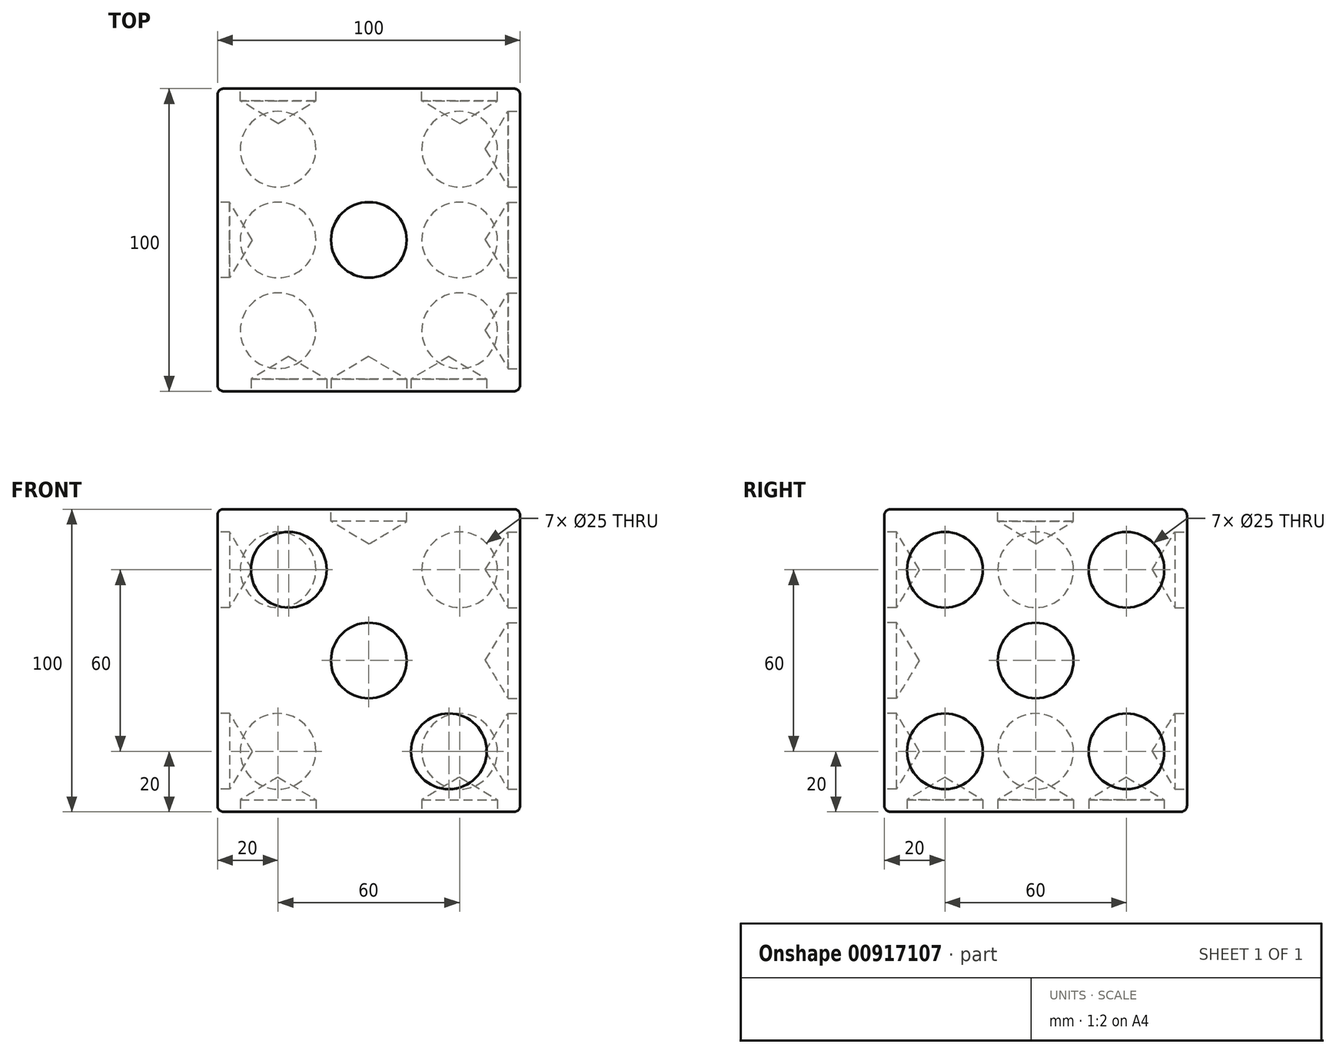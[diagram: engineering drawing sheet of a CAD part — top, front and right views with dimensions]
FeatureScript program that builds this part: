
annotation { "Feature Type Name" : "Feature", "Feature Type Description" : "" }
export const myFeature = defineFeature(function(context is Context, id is Id, definition is map)
    precondition{}
    {
        {
            var Q0;
            Q0=qCreatedBy(makeId("Top.planeOp"),FACE);
            var sketch = newSketch(context, id + "F0", { "sketchPlane" : qUnion([Q0])});
            skLineSegment(sketch, "E0.bottom", {"start": v(50, -50) * mm, "end": v(-50, -50) * mm});
            skLineSegment(sketch, "E0.top", {"start": v(50, 50) * mm, "end": v(-50, 50) * mm});
            skLineSegment(sketch, "E0.left", {"start": v(50, -50) * mm, "end": v(50, 50) * mm});
            skLineSegment(sketch, "E0.right", {"start": v(-50, -50) * mm, "end": v(-50, 50) * mm});
            skPoint(sketch, "E0.middle", {"position": v(0, 0) * mm});
            skSolve(sketch);
        }
        {
            var Q0;
            Q0=makeQuery(id+"F0.imprint","IMPRINT",FACE,{"disambiguationData":[TD([[makeQuery(id+"F0.imprint","IMPRINT",EDGE,{"derivedFrom":sQuery(id+"F0.wireOp",EDGE,"E0.bottom")}),-1.0]])]});
            extrude(context, id + "F1", {"entities" : qUnion([Q0]), "depth" : 100 * mm, "offsetDistance" : 25.4 * mm});
        }
        {
            var Q0;
            Q0=makeQuery(id+"F1.opExtrude","CAP_FACE",FACE,{"disambiguationData":[OSD([sQuery(id+"F0.wireOp",EDGE,"E0.bottom"),sQuery(id+"F0.wireOp",EDGE,"E0.top"),sQuery(id+"F0.wireOp",EDGE,"E0.left"),sQuery(id+"F0.wireOp",EDGE,"E0.right")])],"isStart":false});
            var sketch = newSketch(context, id + "F2", { "sketchPlane" : qUnion([Q0])});
            skCircle(sketch, "E1", {"center": v(0, 0) * mm, "radius": 10 * mm});
            skSolve(sketch);
        }
        {
            var Q0;
            Q0=sQuery(id+"F2.wireOp",VERTEX,"E1.center");
            var Q1;
            Q1=makeQuery(id+"F1.opExtrude","SWEPT_BODY",BODY,{"disambiguationData":[OSD([sQuery(id+"F0.wireOp",EDGE,"E0.bottom"),sQuery(id+"F0.wireOp",EDGE,"E0.top"),sQuery(id+"F0.wireOp",EDGE,"E0.left"),sQuery(id+"F0.wireOp",EDGE,"E0.right")])]});
            hole(context, id + "F3", {"style" : HoleStyle.SIMPLE, "endStyle" : HoleEndStyle.BLIND, "holeDiameter" : 25 * mm, "majorDiameter" : 6.35 * mm, "holeDepth" : 4 * mm, "isTappedThrough" : true, "tappedDepth" : 12.7 * mm, "tapClearance" : 3, "locations" : qUnion([Q0]), "scope" : qUnion([Q1])});
        }
        {
            var Q0;
            Q0=makeQuery(id+"F1.opExtrude","SWEPT_FACE",FACE,{"disambiguationData":[OSD([sQuery(id+"F0.wireOp",EDGE,"E0.top")])]});
            var sketch = newSketch(context, id + "F4", { "sketchPlane" : qUnion([Q0])});
            skCircle(sketch, "E2", {"center": v(-30, 80) * mm, "radius": 12.5 * mm});
            skCircle(sketch, "E3", {"center": v(-30, 20) * mm, "radius": 12.5 * mm});
            skCircle(sketch, "E4", {"center": v(30, 20) * mm, "radius": 12.5 * mm});
            skCircle(sketch, "E5", {"center": v(30, 80) * mm, "radius": 12.5 * mm});
            skSolve(sketch);
        }
        {
            var Q0;
            Q0=sQuery(id+"F4.wireOp",VERTEX,"E2.center");
            var Q1;
            Q1=sQuery(id+"F4.wireOp",VERTEX,"E5.center");
            var Q2;
            Q2=sQuery(id+"F4.wireOp",VERTEX,"E4.center");
            var Q3;
            Q3=sQuery(id+"F4.wireOp",VERTEX,"E3.center");
            var Q4;
            Q4=makeQuery(id+"F1.opExtrude","SWEPT_BODY",BODY,{"disambiguationData":[OSD([sQuery(id+"F0.wireOp",EDGE,"E0.bottom"),sQuery(id+"F0.wireOp",EDGE,"E0.top"),sQuery(id+"F0.wireOp",EDGE,"E0.left"),sQuery(id+"F0.wireOp",EDGE,"E0.right")])]});
            hole(context, id + "F5", {"style" : HoleStyle.SIMPLE, "endStyle" : HoleEndStyle.BLIND, "holeDiameter" : 25 * mm, "majorDiameter" : 6.35 * mm, "holeDepth" : 4 * mm, "isTappedThrough" : true, "tappedDepth" : 12.7 * mm, "tapClearance" : 3, "locations" : qUnion([Q0, Q1, Q2, Q3]), "scope" : qUnion([Q4])});
        }
        {
            var Q0;
            Q0=makeQuery(id+"F1.opExtrude","SWEPT_FACE",FACE,{"disambiguationData":[OSD([sQuery(id+"F0.wireOp",EDGE,"E0.left")])]});
            var sketch = newSketch(context, id + "F6", { "sketchPlane" : qUnion([Q0])});
            skSolve(sketch);
        }
        {
            var Q0;
            Q0=makeQuery(id+"F1.opExtrude","SWEPT_FACE",FACE,{"disambiguationData":[OSD([sQuery(id+"F0.wireOp",EDGE,"E0.right")])]});
            var sketch = newSketch(context, id + "F7", { "sketchPlane" : qUnion([Q0])});
            skCircle(sketch, "E6", {"center": v(0, 80) * mm, "radius": 12.5 * mm});
            skCircle(sketch, "E7", {"center": v(0, 20) * mm, "radius": 12.5 * mm});
            skSolve(sketch);
        }
        {
            var Q0;
            Q0=sQuery(id+"F7.wireOp",VERTEX,"E6.center");
            var Q1;
            Q1=sQuery(id+"F7.wireOp",VERTEX,"E7.center");
            var Q2;
            Q2=makeQuery(id+"F1.opExtrude","SWEPT_BODY",BODY,{"disambiguationData":[OSD([sQuery(id+"F0.wireOp",EDGE,"E0.bottom"),sQuery(id+"F0.wireOp",EDGE,"E0.top"),sQuery(id+"F0.wireOp",EDGE,"E0.left"),sQuery(id+"F0.wireOp",EDGE,"E0.right")])]});
            hole(context, id + "F8", {"style" : HoleStyle.SIMPLE, "endStyle" : HoleEndStyle.BLIND, "holeDiameter" : 25 * mm, "majorDiameter" : 6.35 * mm, "holeDepth" : 4 * mm, "isTappedThrough" : true, "tappedDepth" : 12.7 * mm, "tapClearance" : 3, "locations" : qUnion([Q0, Q1]), "scope" : qUnion([Q2])});
        }
        {
            var Q0;
            Q0=makeQuery(id+"F1.opExtrude","CAP_FACE",FACE,{"disambiguationData":[OSD([sQuery(id+"F0.wireOp",EDGE,"E0.bottom"),sQuery(id+"F0.wireOp",EDGE,"E0.top"),sQuery(id+"F0.wireOp",EDGE,"E0.left"),sQuery(id+"F0.wireOp",EDGE,"E0.right")])],"isStart":true});
            var sketch = newSketch(context, id + "F9", { "sketchPlane" : qUnion([Q0])});
            skCircle(sketch, "E8", {"center": v(30, -30) * mm, "radius": 12.5 * mm});
            skCircle(sketch, "E9", {"center": v(30, 0) * mm, "radius": 12.5 * mm});
            skCircle(sketch, "E10", {"center": v(30, 30) * mm, "radius": 12.5 * mm});
            skCircle(sketch, "E11", {"center": v(-30, -30) * mm, "radius": 12.5 * mm});
            skCircle(sketch, "E12", {"center": v(-30, 0) * mm, "radius": 12.5 * mm});
            skCircle(sketch, "E13", {"center": v(-30, 30) * mm, "radius": 12.5 * mm});
            skSolve(sketch);
        }
        {
            var Q0;
            Q0=sQuery(id+"F9.wireOp",VERTEX,"E8.center");
            var Q1;
            Q1=sQuery(id+"F9.wireOp",VERTEX,"E9.center");
            var Q2;
            Q2=sQuery(id+"F9.wireOp",VERTEX,"E10.center");
            var Q3;
            Q3=sQuery(id+"F9.wireOp",VERTEX,"E11.center");
            var Q4;
            Q4=sQuery(id+"F9.wireOp",VERTEX,"E12.center");
            var Q5;
            Q5=sQuery(id+"F9.wireOp",VERTEX,"E13.center");
            var Q6;
            Q6=makeQuery(id+"F1.opExtrude","SWEPT_BODY",BODY,{"disambiguationData":[OSD([sQuery(id+"F0.wireOp",EDGE,"E0.bottom"),sQuery(id+"F0.wireOp",EDGE,"E0.top"),sQuery(id+"F0.wireOp",EDGE,"E0.left"),sQuery(id+"F0.wireOp",EDGE,"E0.right")])]});
            hole(context, id + "F10", {"style" : HoleStyle.SIMPLE, "endStyle" : HoleEndStyle.BLIND, "holeDiameter" : 25 * mm, "majorDiameter" : 6.35 * mm, "holeDepth" : 4 * mm, "isTappedThrough" : true, "tappedDepth" : 12.7 * mm, "tapClearance" : 3, "locations" : qUnion([Q0, Q1, Q2, Q3, Q4, Q5]), "scope" : qUnion([Q6])});
        }
        {
            var Q0;
            Q0=makeQuery(id+"F1.opExtrude","SWEPT_FACE",FACE,{"disambiguationData":[OSD([sQuery(id+"F0.wireOp",EDGE,"E0.bottom")])]});
            var sketch = newSketch(context, id + "F11", { "sketchPlane" : qUnion([Q0])});
            skCircle(sketch, "E14", {"center": v(26.46, 20) * mm, "radius": 12.5 * mm});
            skCircle(sketch, "E15", {"center": v(0, 50) * mm, "radius": 12.5 * mm});
            skCircle(sketch, "E16", {"center": v(-26.46, 80) * mm, "radius": 12.5 * mm});
            skSolve(sketch);
        }
        {
            var Q0;
            Q0=sQuery(id+"F11.wireOp",VERTEX,"E14.center");
            var Q1;
            Q1=sQuery(id+"F11.wireOp",VERTEX,"E15.center");
            var Q2;
            Q2=sQuery(id+"F11.wireOp",VERTEX,"E16.center");
            var Q3;
            Q3=makeQuery(id+"F1.opExtrude","SWEPT_BODY",BODY,{"disambiguationData":[OSD([sQuery(id+"F0.wireOp",EDGE,"E0.bottom"),sQuery(id+"F0.wireOp",EDGE,"E0.top"),sQuery(id+"F0.wireOp",EDGE,"E0.left"),sQuery(id+"F0.wireOp",EDGE,"E0.right")])]});
            hole(context, id + "F12", {"style" : HoleStyle.SIMPLE, "endStyle" : HoleEndStyle.BLIND, "holeDiameter" : 25 * mm, "majorDiameter" : 6.35 * mm, "holeDepth" : 4 * mm, "isTappedThrough" : true, "tappedDepth" : 12.7 * mm, "tapClearance" : 3, "locations" : qUnion([Q0, Q1, Q2]), "scope" : qUnion([Q3])});
        }
        {
            var Q0;
            {var subQ0=sQuery(id+"F0.wireOp",EDGE,"E0.left");Q0=makeQuery(id+"F6.imprint","IMPRINT",FACE,{"disambiguationData":[TD([[makeQuery(id+"F6.imprint","IMPRINT",EDGE,{"derivedFrom":makeQuery(id+"F1.opExtrude","CAP_EDGE",EDGE,{"disambiguationData":[OSD([subQ0])],"isStart":true})}),1.0]])]});}
            var sketch = newSketch(context, id + "F13", { "sketchPlane" : qUnion([Q0])});
            skCircle(sketch, "E17", {"center": v(0, 50) * mm, "radius": 12.5 * mm});
            skCircle(sketch, "E18", {"center": v(30, 20) * mm, "radius": 12.5 * mm});
            skCircle(sketch, "E19", {"center": v(-30, 20) * mm, "radius": 12.5 * mm});
            skCircle(sketch, "E20", {"center": v(-30, 80) * mm, "radius": 12.5 * mm});
            skCircle(sketch, "E21", {"center": v(30, 80) * mm, "radius": 12.5 * mm});
            skSolve(sketch);
        }
        {
            var Q0;
            Q0=sQuery(id+"F13.wireOp",VERTEX,"E18.center");
            var Q1;
            Q1=sQuery(id+"F13.wireOp",VERTEX,"E19.center");
            var Q2;
            Q2=sQuery(id+"F13.wireOp",VERTEX,"E17.center");
            var Q3;
            Q3=sQuery(id+"F13.wireOp",VERTEX,"E20.center");
            var Q4;
            Q4=sQuery(id+"F13.wireOp",VERTEX,"E21.center");
            var Q5;
            Q5=makeQuery(id+"F1.opExtrude","SWEPT_BODY",BODY,{"disambiguationData":[OSD([sQuery(id+"F0.wireOp",EDGE,"E0.bottom"),sQuery(id+"F0.wireOp",EDGE,"E0.top"),sQuery(id+"F0.wireOp",EDGE,"E0.left"),sQuery(id+"F0.wireOp",EDGE,"E0.right")])]});
            hole(context, id + "F14", {"style" : HoleStyle.SIMPLE, "endStyle" : HoleEndStyle.BLIND, "holeDiameter" : 25 * mm, "majorDiameter" : 6.35 * mm, "holeDepth" : 4 * mm, "isTappedThrough" : true, "tappedDepth" : 12.7 * mm, "tapClearance" : 3, "locations" : qUnion([Q0, Q1, Q2, Q3, Q4]), "scope" : qUnion([Q5])});
        }
        {
            var Q0;
            Q0=makeQuery(id+"F1.opExtrude","CAP_EDGE",EDGE,{"disambiguationData":[OSD([sQuery(id+"F0.wireOp",EDGE,"E0.top")])],"isStart":true});
            fillet(context, id + "F15", {"entities" : qUnion([Q0]), "radius" : 2 * mm, "tangentPropagation" : true, "allowEdgeOverflow" : false});
        }
        {
            var Q0;
            Q0=makeQuery(id+"F1.opExtrude","CAP_EDGE",EDGE,{"disambiguationData":[OSD([sQuery(id+"F0.wireOp",EDGE,"E0.left")])],"isStart":true});
            var Q1;
            Q1=makeQuery(id+"F1.opExtrude","SWEPT_EDGE",EDGE,{"disambiguationData":[OSD([sQuery(id+"F0.wireOp",EDGE,"E0.top"),sQuery(id+"F0.wireOp",EDGE,"E0.left")])]});
            var Q2;
            Q2=makeQuery(id+"F1.opExtrude","CAP_EDGE",EDGE,{"disambiguationData":[OSD([sQuery(id+"F0.wireOp",EDGE,"E0.left")])],"isStart":false});
            var Q3;
            Q3=makeQuery(id+"F1.opExtrude","CAP_EDGE",EDGE,{"disambiguationData":[OSD([sQuery(id+"F0.wireOp",EDGE,"E0.top")])],"isStart":false});
            var Q4;
            Q4=makeQuery(id+"F1.opExtrude","CAP_EDGE",EDGE,{"disambiguationData":[OSD([sQuery(id+"F0.wireOp",EDGE,"E0.right")])],"isStart":false});
            var Q5;
            Q5=makeQuery(id+"F1.opExtrude","SWEPT_EDGE",EDGE,{"disambiguationData":[OSD([sQuery(id+"F0.wireOp",EDGE,"E0.top"),sQuery(id+"F0.wireOp",EDGE,"E0.right")])]});
            var Q6;
            Q6=makeQuery(id+"F1.opExtrude","CAP_EDGE",EDGE,{"disambiguationData":[OSD([sQuery(id+"F0.wireOp",EDGE,"E0.bottom")])],"isStart":false});
            var Q7;
            Q7=makeQuery(id+"F1.opExtrude","SWEPT_EDGE",EDGE,{"disambiguationData":[OSD([sQuery(id+"F0.wireOp",EDGE,"E0.bottom"),sQuery(id+"F0.wireOp",EDGE,"E0.right")])]});
            var Q8;
            Q8=makeQuery(id+"F1.opExtrude","CAP_EDGE",EDGE,{"disambiguationData":[OSD([sQuery(id+"F0.wireOp",EDGE,"E0.bottom")])],"isStart":true});
            var Q9;
            Q9=makeQuery(id+"F1.opExtrude","SWEPT_EDGE",EDGE,{"disambiguationData":[OSD([sQuery(id+"F0.wireOp",EDGE,"E0.bottom"),sQuery(id+"F0.wireOp",EDGE,"E0.left")])]});
            fillet(context, id + "F16", {"entities" : qUnion([Q0, Q1, Q2, Q3, Q4, Q5, Q6, Q7, Q8, Q9]), "radius" : 2 * mm, "tangentPropagation" : true, "allowEdgeOverflow" : false});
        }
    });
